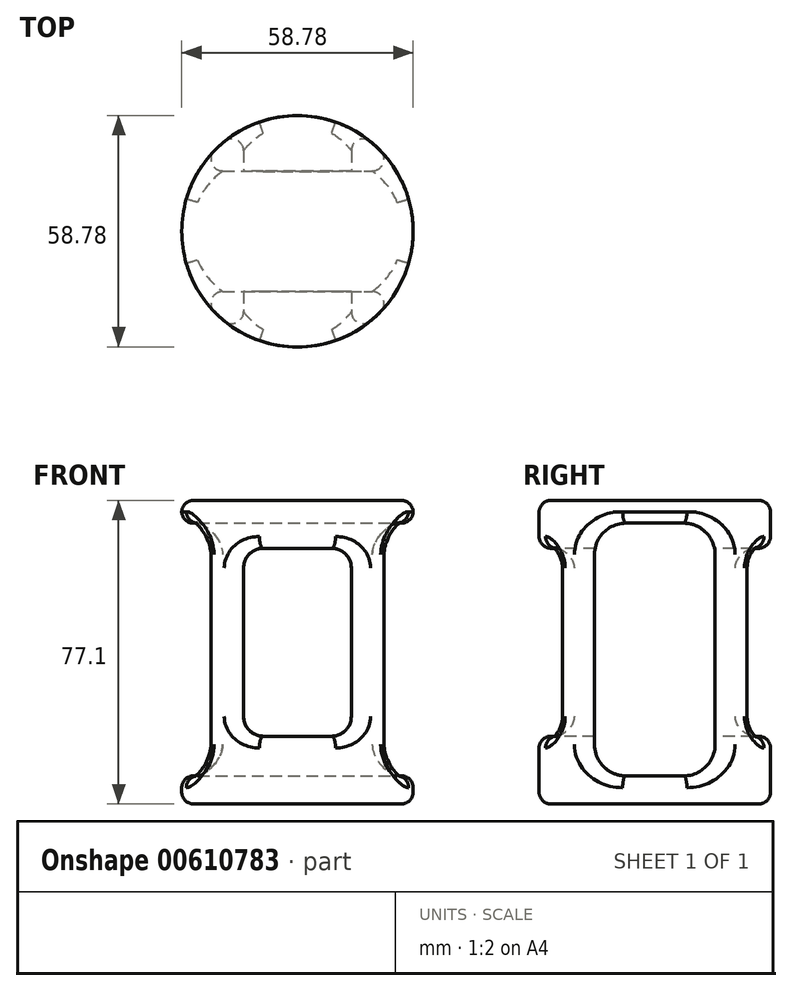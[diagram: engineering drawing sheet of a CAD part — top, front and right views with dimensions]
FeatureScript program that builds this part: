
annotation { "Feature Type Name" : "Feature", "Feature Type Description" : "" }
export const myFeature = defineFeature(function(context is Context, id is Id, definition is map)
    precondition{}
    {
        {
            var Q0;
            Q0=qCreatedBy(makeId("Top.planeOp"),FACE);
            var sketch = newSketch(context, id + "F0", { "sketchPlane" : qUnion([Q0])});
            skCircle(sketch, "E0", {"center": v(0, 0) * mm, "radius": 29.4 * mm});
            skSolve(sketch);
        }
        {
            var Q0;
            Q0=makeQuery(id+"F0.imprint","IMPRINT",FACE,{"disambiguationData":[TD([[makeQuery(id+"F0.imprint","IMPRINT",EDGE,{"derivedFrom":sQuery(id+"F0.wireOp",EDGE,"E0")}),1.0]])]});
            extrude(context, id + "F1", {"entities" : qUnion([Q0]), "depth" : 77.1 * mm, "offsetDistance" : 25 * mm});
        }
        {
            var Q0;
            Q0=qCreatedBy(makeId("Front.planeOp"),FACE);
            var sketch = newSketch(context, id + "F2", { "sketchPlane" : qUnion([Q0])});
            skLineSegment(sketch, "E1.bottom", {"start": v(8.69, 17.2) * mm, "end": v(-8.69, 17.2) * mm});
            skLineSegment(sketch, "E1.top", {"start": v(8.69, 64.95) * mm, "end": v(-8.69, 64.95) * mm});
            skLineSegment(sketch, "E1.left", {"start": v(13.69, 22.2) * mm, "end": v(13.69, 59.95) * mm});
            skLineSegment(sketch, "E1.right", {"start": v(-13.69, 22.2) * mm, "end": v(-13.69, 59.95) * mm});
            skPoint(sketch, "E1.middle", {"position": v(0, 41.08) * mm});
            skPoint(sketch, "E2.visualSharp", {"position": v(13.69, 64.95) * mm});
            skArc(sketch, "E2.filletArc", {"start": v(13.69, 59.95) * mm, "mid": v(12.22, 63.49) * mm, "end": v(8.69, 64.95) * mm});
            skPoint(sketch, "E3.visualSharp", {"position": v(-13.69, 64.95) * mm});
            skArc(sketch, "E3.filletArc", {"start": v(-8.69, 64.95) * mm, "mid": v(-12.22, 63.49) * mm, "end": v(-13.69, 59.95) * mm});
            skPoint(sketch, "E4.visualSharp", {"position": v(-13.69, 17.2) * mm});
            skArc(sketch, "E4.filletArc", {"start": v(-13.69, 22.2) * mm, "mid": v(-12.22, 18.67) * mm, "end": v(-8.69, 17.2) * mm});
            skPoint(sketch, "E5.visualSharp", {"position": v(13.69, 17.2) * mm});
            skArc(sketch, "E5.filletArc", {"start": v(8.69, 17.2) * mm, "mid": v(12.22, 18.67) * mm, "end": v(13.69, 22.2) * mm});
            skSolve(sketch);
        }
        {
            var Q0;
            Q0=makeQuery(id+"F2.imprint","IMPRINT",FACE,{"disambiguationData":[TD([[makeQuery(id+"F2.imprint","IMPRINT",EDGE,{"derivedFrom":sQuery(id+"F2.wireOp",EDGE,"E1.bottom")}),-1.0]])]});
            extrude(context, id + "F3", {"entities" : qUnion([Q0]), "operationType" : NewBodyOperationType.REMOVE, "oppositeDirection" : true, "depth" : 93.8 * mm, "offsetDistance" : 25 * mm, "hasSecondDirection" : true, "secondDirectionOppositeDirection" : false, "secondDirectionDepth" : 86.1 * mm});
        }
        {
            var Q0;
            Q0=qCreatedBy(makeId("Right.planeOp"),FACE);
            var sketch = newSketch(context, id + "F4", { "sketchPlane" : qUnion([Q0])});
            skLineSegment(sketch, "E6.bottom", {"start": v(7.33, 7.12) * mm, "end": v(-7.33, 7.12) * mm});
            skLineSegment(sketch, "E6.top", {"start": v(7.33, 71.33) * mm, "end": v(-7.33, 71.33) * mm});
            skLineSegment(sketch, "E6.left", {"start": v(15.33, 15.12) * mm, "end": v(15.33, 63.33) * mm});
            skLineSegment(sketch, "E6.right", {"start": v(-15.33, 15.12) * mm, "end": v(-15.33, 63.33) * mm});
            skPoint(sketch, "E6.middle", {"position": v(0, 39.23) * mm});
            skPoint(sketch, "E7.visualSharp", {"position": v(-15.33, 71.33) * mm});
            skArc(sketch, "E7.filletArc", {"start": v(-7.33, 71.33) * mm, "mid": v(-12.99, 68.99) * mm, "end": v(-15.33, 63.33) * mm});
            skPoint(sketch, "E8.visualSharp", {"position": v(15.33, 71.33) * mm});
            skArc(sketch, "E8.filletArc", {"start": v(15.33, 63.33) * mm, "mid": v(12.99, 68.99) * mm, "end": v(7.33, 71.33) * mm});
            skPoint(sketch, "E9.visualSharp", {"position": v(15.33, 7.12) * mm});
            skArc(sketch, "E9.filletArc", {"start": v(7.33, 7.12) * mm, "mid": v(12.99, 9.46) * mm, "end": v(15.33, 15.12) * mm});
            skPoint(sketch, "E10.visualSharp", {"position": v(-15.33, 7.12) * mm});
            skArc(sketch, "E10.filletArc", {"start": v(-15.33, 15.12) * mm, "mid": v(-12.99, 9.46) * mm, "end": v(-7.33, 7.12) * mm});
            skSolve(sketch);
        }
        {
            var Q0;
            Q0=makeQuery(id+"F4.imprint","IMPRINT",FACE,{"disambiguationData":[TD([[makeQuery(id+"F4.imprint","IMPRINT",EDGE,{"derivedFrom":sQuery(id+"F4.wireOp",EDGE,"E6.bottom")}),-1.0]])]});
            extrude(context, id + "F5", {"entities" : qUnion([Q0]), "operationType" : NewBodyOperationType.REMOVE, "oppositeDirection" : true, "depth" : 114 * mm, "offsetDistance" : 25 * mm, "hasSecondDirection" : true, "secondDirectionOppositeDirection" : false, "secondDirectionDepth" : 67 * mm});
        }
        {
            var Q0;
            Q0=makeQuery(id+"F1.opExtrude","SWEPT_FACE",FACE,{"disambiguationData":[OSD([sQuery(id+"F0.wireOp",EDGE,"E0")])]});
            fillet(context, id + "F6", {"entities" : qUnion([Q0]), "radius" : 3 * mm, "tangentPropagation" : true, "allowEdgeOverflow" : false});
        }
    });
